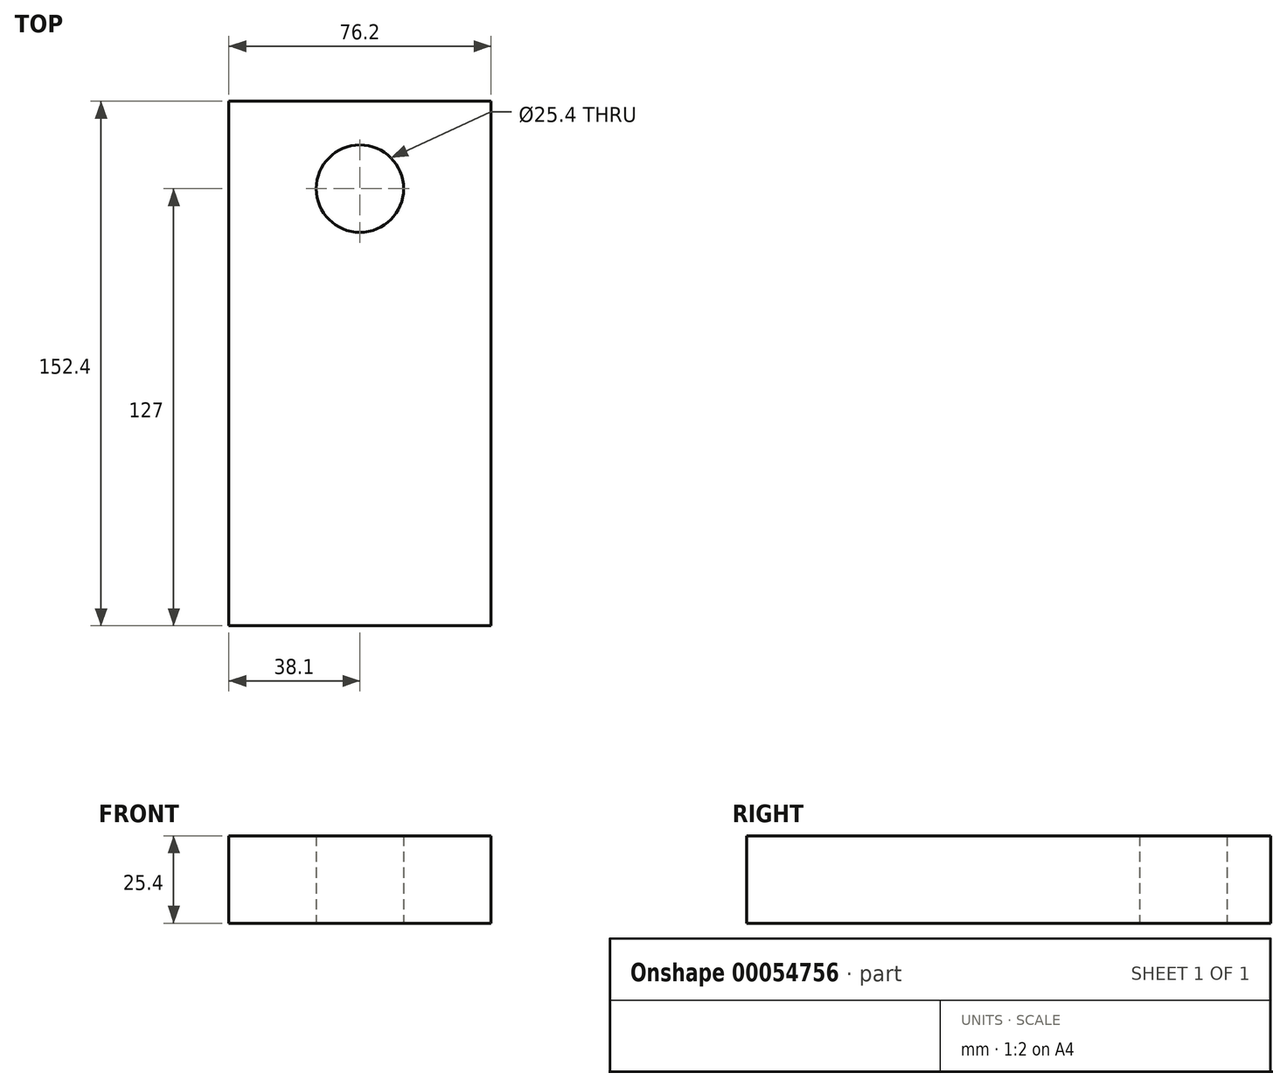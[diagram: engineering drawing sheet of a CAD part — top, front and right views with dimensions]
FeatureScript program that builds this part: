
annotation { "Feature Type Name" : "Feature", "Feature Type Description" : "" }
export const myFeature = defineFeature(function(context is Context, id is Id, definition is map)
    precondition{}
    {
        {
            var Q0;
            Q0=qCreatedBy(makeId("Top.planeOp"),FACE);
            var sketch = newSketch(context, id + "F0", { "sketchPlane" : qUnion([Q0])});
            skLineSegment(sketch, "E0.rect.bottom", {"start": v(38.1, 76.2) * mm, "end": v(-38.1, 76.2) * mm});
            skLineSegment(sketch, "E0.rect.top", {"start": v(38.1, -76.2) * mm, "end": v(-38.1, -76.2) * mm});
            skLineSegment(sketch, "E0.rect.left", {"start": v(38.1, 76.2) * mm, "end": v(38.1, -76.2) * mm});
            skLineSegment(sketch, "E0.rect.right", {"start": v(-38.1, 76.2) * mm, "end": v(-38.1, -76.2) * mm});
            skPoint(sketch, "E0.rect.middle", {"position": v(0, 0) * mm});
            skCircle(sketch, "E1", {"center": v(0, 50.8) * mm, "radius": 12.7 * mm});
            skSolve(sketch);
        }
        {
            var Q0;
            Q0=makeQuery(id+"F0.imprint","IMPRINT",FACE,{"disambiguationData":[TD([[makeQuery(id+"F0.imprint","IMPRINT",EDGE,{"derivedFrom":sQuery(id+"F0.wireOp",EDGE,"E0.rect.bottom")}),1.0]])]});
            extrude(context, id + "F1", {"entities" : qUnion([Q0]), "depth" : 25.4 * mm});
        }
    });
